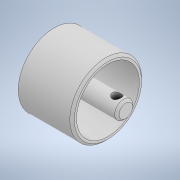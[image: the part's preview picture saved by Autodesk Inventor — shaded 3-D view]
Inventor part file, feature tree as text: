
AUTODESK INVENTOR PART (.ipt)
format: ipt  version: 2021 (Build 250183000, 183)  size: 131,072 bytes
history: native  units: mm
features: extrude x4, sketch x4, chamfer x1
ambient origin geometry x8: Origin, YZ Plane, XZ Plane, XY Plane, X Axis, Y Axis, Z Axis, Center Point
bodies: Solid1 (feature_tree)
feature tree (9):
  extrude  "Extrusion1"  Depth=19.05mm TaperAngle=0.0deg
  extrude  "Extrusion2"  Depth=15.875mm TaperAngle=0.0deg
  extrude  "Extrusion3"  Depth=6.35mm TaperAngle=0.0deg
  extrude  "Extrusion4"  Depth=3.175mm
  chamfer  "Chamfer1"  Distance=22.225mm
  sketch  "Sketch1"  dims[d0=25.4mm d1=19.05mm d2=0.0mm]
  sketch  "Sketch2"  dims[d3=22.225mm d4=15.875mm d5=0.0mm]
  sketch  "Sketch3"  dims[d6=6.35mm d7=22.225mm d8=0.0mm]
  sketch  "Sketch4"  dims[d9=3.175mm d10=3.175mm d11=22.225mm d12=0.0mm d13=0.79375mm d14=3.175mm d15=45.0deg]
